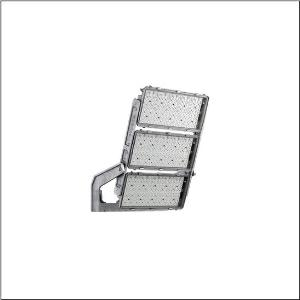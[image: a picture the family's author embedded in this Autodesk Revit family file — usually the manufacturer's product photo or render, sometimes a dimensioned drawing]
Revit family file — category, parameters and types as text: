
# Revit family: floodlight_fl_11_maxi_pro_remote___pl33tblc_5xa779426h01aa_354a
name_source: partatom
category: Lighting Fixtures
units: mm (PartAtom-declared; Revit-internal decimal feet)

## family parameters
Cut with Voids When Loaded = No
Host = Face
Light Source = No
Part Type = Normal
Room Calculation Point = No
Round Connector Dimension = Use Diameter
Shared = No

## types (1)
- --- (1 x LED, 124720 lm, 1388.3 W, 4000K)
    Apparent Load = 1388 VA
    CIE Flux Codes = 24 77 100 100 100
    Color Rendering = 70
    Color Temperature = 4000K
    Default Elevation = 1800 mm
    Description = Floodlight FL 11  maxi  pro Remote floodlight; light control with lens of PMMA; cover panel of toughened safety glass, transparent; light distribution: PL33TBLC, asymmetric direct distribution, LEDcolour temperature: 4000K, rated luminous flux: 124.720lm, colour rendering: CRI > 70, light colour: 740; luminous efficacy: 90lm/W; brightness control: DALI 2 (1 DALI address); with terminal, 8-pole, max. 2.5mm², mains connection: 220..240V/380..400V AC, 50/60Hz, surge voltage resistance: line to ground: 10kV, ECG replaceable separately, LED unit replaceable without ESD environment, dustproof LED module, dimming range 10..100%, no afterglow with DALI off / DMX off command; 1388W floodlight with 2x LED unit of diecast aluminium, coated grey; length: 713mm / width: 651mm / height: 338mm; mounting bracket, of diecast aluminium, uncoated, natural, equipment: Power, protection rating (complete): IP66; insulation class (complete): insulation class I (protective earthing); certification: CE, ENEC, VDE; ball protection: ball impact resistance with accessories, impact resistance: IK07; rated ambient temperature 10°C, only for outdoor installations, permissible operating ambient temperature: -40..+30°C, permissible storage temperature: -40..+85°C; packaging unit: 1 piece

Light Distribution: PL33TBLC
    Height = 320 mm
    Lamp = 1 x LED
    Lamp Light Flux = 124720 lm
    Lamp Power = 1388.3 W
    Lamp count = 1
    Length = 1002 mm
    Luminous efficacy = 90 lm/W
    Manufacturer = Siteco
    ModVariant = No
    Model = 5XA779426H01AA
    Mounting Place = Ceiling
    Mounting Type = Surface mounted
    Number of Poles = 1
    OnlyDefault = Yes
    Power Factor = 1
    Product Name = Floodlight FL 11 maxi pro Remote | PL33TBLC
    Product group = floodlight | ceiling mounted
    ProductGroupID = 303
    Protection Class = Protection class I
    Protection Degree = IP 66
    RLX_Detail_Level = 1
    RLX_Emergency_Light_Flux = 0 lm
    RLX_Emergency_Type = 0
    RLX_Emergency_Type_DB = No
    RlxData = <blob elided: 52061 chars, md5=9995c983>
    Socket = socket
    Standby Power = 0 W
    System Light Flux = 124720 lm
    System Power = 1388 W
    Type Comments = factory setting: luminous flux: 100 % | dim-lin: 254 | 955 mA
    Type Image = l_1006784.jpg
    URL = http://relux.com
    VarID = @adj_044627
    Voltage = 0 V
    Weight = 0.00 kg
    Width = 655 mm

## geometry (parser evidence)
native form markers: Blend x4, Sweep x13
no freeform markers — native parametric forms only
